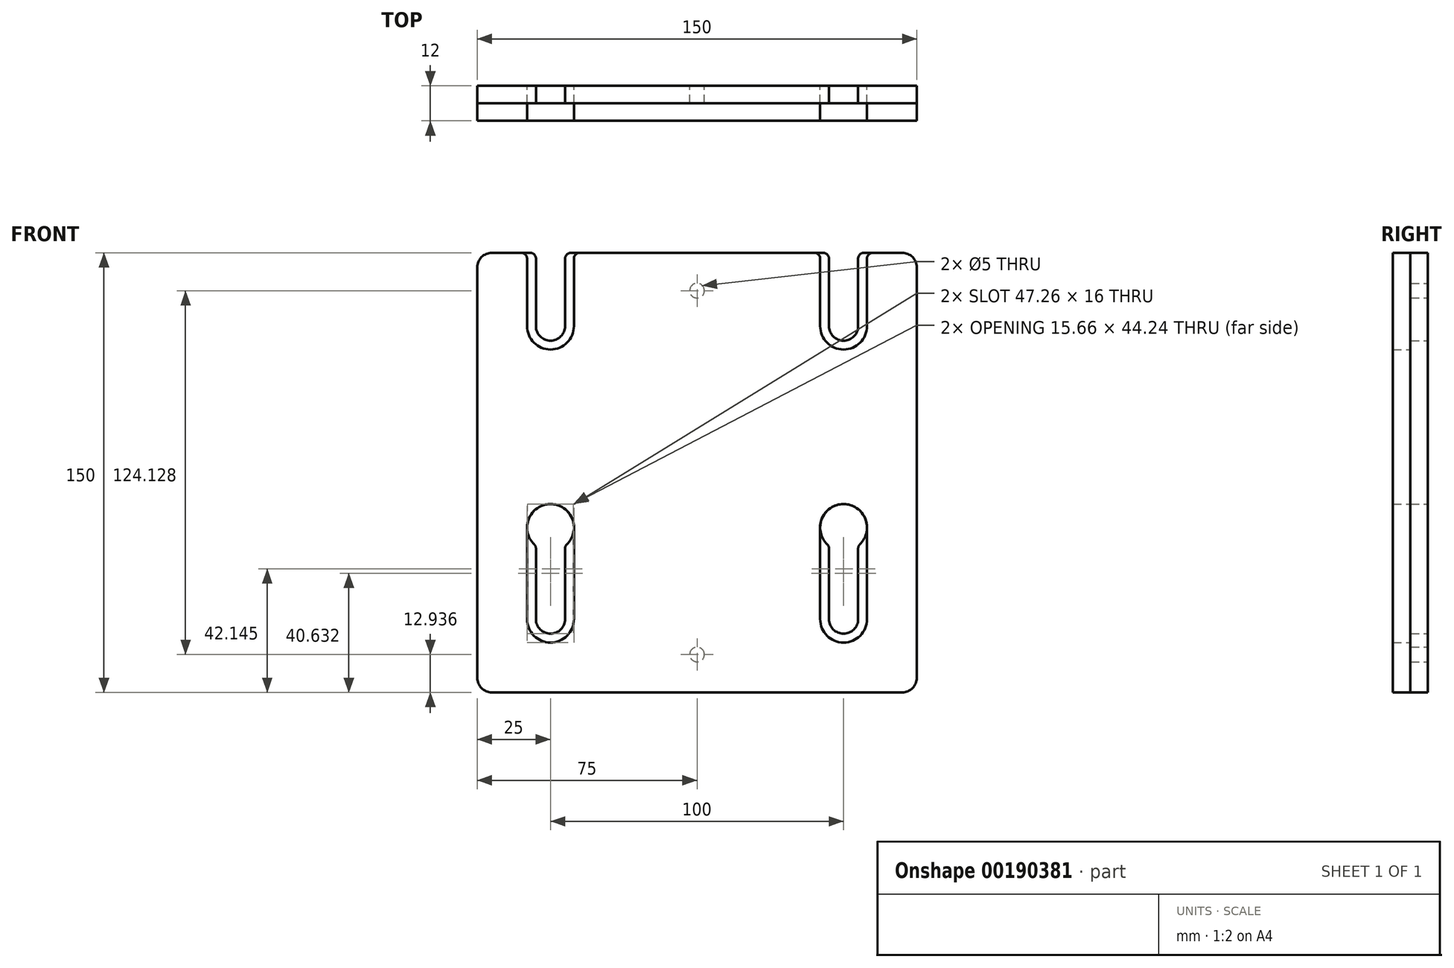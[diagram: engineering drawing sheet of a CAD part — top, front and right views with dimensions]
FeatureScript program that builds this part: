
annotation { "Feature Type Name" : "Feature", "Feature Type Description" : "" }
export const myFeature = defineFeature(function(context is Context, id is Id, definition is map)
    precondition{}
    {
        {
            var Q0;
            Q0=qCreatedBy(makeId("Front.planeOp"),FACE);
            var sketch = newSketch(context, id + "F0", { "sketchPlane" : qUnion([Q0])});
            skLineSegment(sketch, "E0.bottom", {"start": v(70, -75) * mm, "end": v(-70, -75) * mm});
            skLineSegment(sketch, "E0.top", {"start": v(70, 75) * mm, "end": v(56.98, 75) * mm});
            skLineSegment(sketch, "E0.left", {"start": v(75, -70) * mm, "end": v(75, 70) * mm});
            skLineSegment(sketch, "E0.right", {"start": v(-75, -70) * mm, "end": v(-75, 70) * mm});
            skPoint(sketch, "E0.middle", {"position": v(0, 0) * mm});
            skArc(sketch, "E1", {"start": v(-54.98, 50) * mm, "mid": v(-50, 45.03) * mm, "end": v(-45.03, 50) * mm});
            skArc(sketch, "E2.MirrorC", {"start": v(54.98, 50) * mm, "mid": v(50, 45.03) * mm, "end": v(45.03, 50) * mm});
            skArc(sketch, "E3.MirrorC", {"start": v(-45.03, -50) * mm, "mid": v(-50, -54.98) * mm, "end": v(-54.98, -50) * mm});
            skArc(sketch, "E4.MirrorC", {"start": v(45.03, -50) * mm, "mid": v(50, -54.98) * mm, "end": v(54.98, -50) * mm});
            skPoint(sketch, "E5.visualSharp", {"position": v(-75, 75) * mm});
            skArc(sketch, "E5.filletArc", {"start": v(-70, 75) * mm, "mid": v(-73.54, 73.54) * mm, "end": v(-75, 70) * mm});
            skPoint(sketch, "E6.visualSharp", {"position": v(-75, -75) * mm});
            skArc(sketch, "E6.filletArc", {"start": v(-75, -70) * mm, "mid": v(-73.54, -73.54) * mm, "end": v(-70, -75) * mm});
            skPoint(sketch, "E7.visualSharp", {"position": v(75, -75) * mm});
            skArc(sketch, "E7.filletArc", {"start": v(70, -75) * mm, "mid": v(73.54, -73.54) * mm, "end": v(75, -70) * mm});
            skLineSegment(sketch, "E8", {"start": v(-45.03, 50) * mm, "end": v(-45.03, 73) * mm});
            skLineSegment(sketch, "E9", {"start": v(-54.98, 50) * mm, "end": v(-54.98, 73) * mm});
            skArc(sketch, "E10", {"start": v(-44.42, -24.47) * mm, "mid": v(-50, -10.74) * mm, "end": v(-55.58, -24.47) * mm});
            skLineSegment(sketch, "E11", {"start": v(-45.03, -50) * mm, "end": v(-45.03, -25.9) * mm});
            skLineSegment(sketch, "E12", {"start": v(-54.98, -50) * mm, "end": v(-54.98, -25.9) * mm});
            skLineSegment(sketch, "E13.MirrorCS", {"start": v(45.03, 50) * mm, "end": v(45.03, 73) * mm});
            skLineSegment(sketch, "E14.MirrorCS", {"start": v(54.98, 50) * mm, "end": v(54.98, 73) * mm});
            skArc(sketch, "E15.MirrorCS", {"start": v(44.42, -24.47) * mm, "mid": v(50, -10.74) * mm, "end": v(55.58, -24.47) * mm});
            skLineSegment(sketch, "E16.MirrorCS", {"start": v(45.03, -50) * mm, "end": v(45.03, -25.9) * mm});
            skLineSegment(sketch, "E17.MirrorCS", {"start": v(54.98, -50) * mm, "end": v(54.98, -25.9) * mm});
            skLineSegment(sketch, "E18.trimOffspring", {"start": v(-56.98, 75) * mm, "end": v(-70, 75) * mm});
            skLineSegment(sketch, "E19.trimOffspring", {"start": v(43.03, 75) * mm, "end": v(-43.03, 75) * mm});
            skPoint(sketch, "E20.visualSharp", {"position": v(-54.98, 75) * mm});
            skArc(sketch, "E20.filletArc", {"start": v(-54.98, 73) * mm, "mid": v(-55.56, 74.41) * mm, "end": v(-56.98, 75) * mm});
            skPoint(sketch, "E21.visualSharp", {"position": v(-45.03, 75) * mm});
            skArc(sketch, "E21.filletArc", {"start": v(-43.03, 75) * mm, "mid": v(-44.44, 74.41) * mm, "end": v(-45.03, 73) * mm});
            skPoint(sketch, "E22.visualSharp", {"position": v(45.03, 75) * mm});
            skArc(sketch, "E22.filletArc", {"start": v(45.03, 73) * mm, "mid": v(44.44, 74.41) * mm, "end": v(43.03, 75) * mm});
            skPoint(sketch, "E23.visualSharp", {"position": v(54.98, 75) * mm});
            skArc(sketch, "E23.filletArc", {"start": v(56.98, 75) * mm, "mid": v(55.56, 74.41) * mm, "end": v(54.98, 73) * mm});
            skPoint(sketch, "E24.visualSharp", {"position": v(75, 75) * mm});
            skArc(sketch, "E24.filletArc", {"start": v(75, 70) * mm, "mid": v(73.54, 73.54) * mm, "end": v(70, 75) * mm});
            skPoint(sketch, "E25.visualSharp", {"position": v(-54.98, -25) * mm});
            skArc(sketch, "E25.filletArc", {"start": v(-54.98, -25.9) * mm, "mid": v(-55.13, -25.12) * mm, "end": v(-55.58, -24.47) * mm});
            skPoint(sketch, "E26.visualSharp", {"position": v(-45.03, -25) * mm});
            skArc(sketch, "E26.filletArc", {"start": v(-44.42, -24.47) * mm, "mid": v(-44.87, -25.12) * mm, "end": v(-45.03, -25.9) * mm});
            skPoint(sketch, "E27.visualSharp", {"position": v(45.03, -25) * mm});
            skArc(sketch, "E27.filletArc", {"start": v(45.03, -25.9) * mm, "mid": v(44.87, -25.12) * mm, "end": v(44.42, -24.47) * mm});
            skPoint(sketch, "E28.visualSharp", {"position": v(54.98, -25) * mm});
            skArc(sketch, "E28.filletArc", {"start": v(55.58, -24.47) * mm, "mid": v(55.13, -25.12) * mm, "end": v(54.98, -25.9) * mm});
            skCircle(sketch, "E29", {"center": v(0, 62.06) * mm, "radius": 2.5 * mm});
            skCircle(sketch, "E30.MirrorC", {"center": v(0, -62.06) * mm, "radius": 2.5 * mm});
            skSolve(sketch);
        }
        {
            var Q0;
            Q0 = qSketchRegion(id + "F0", true);
            extrude(context, id + "F1", {"entities" : qUnion([Q0]), "depth" : 6 * mm});
        }
        {
            var Q0;
            Q0=makeQuery(id+"F1.opExtrude","CAP_FACE",FACE,{"disambiguationData":[OSD([sQuery(id+"F0.wireOp",EDGE,"E0.bottom"),sQuery(id+"F0.wireOp",EDGE,"E0.top"),sQuery(id+"F0.wireOp",EDGE,"E0.left"),sQuery(id+"F0.wireOp",EDGE,"E0.right"),sQuery(id+"F0.wireOp",EDGE,"E1"),sQuery(id+"F0.wireOp",EDGE,"E2.MirrorC"),sQuery(id+"F0.wireOp",EDGE,"E3.MirrorC"),sQuery(id+"F0.wireOp",EDGE,"E4.MirrorC"),sQuery(id+"F0.wireOp",EDGE,"E5.filletArc"),sQuery(id+"F0.wireOp",EDGE,"E6.filletArc"),sQuery(id+"F0.wireOp",EDGE,"E7.filletArc"),sQuery(id+"F0.wireOp",EDGE,"E8"),sQuery(id+"F0.wireOp",EDGE,"E9"),sQuery(id+"F0.wireOp",EDGE,"E10"),sQuery(id+"F0.wireOp",EDGE,"E11"),sQuery(id+"F0.wireOp",EDGE,"E12"),sQuery(id+"F0.wireOp",EDGE,"E13.MirrorCS"),sQuery(id+"F0.wireOp",EDGE,"E14.MirrorCS"),sQuery(id+"F0.wireOp",EDGE,"E15.MirrorCS"),sQuery(id+"F0.wireOp",EDGE,"E16.MirrorCS"),sQuery(id+"F0.wireOp",EDGE,"E17.MirrorCS"),sQuery(id+"F0.wireOp",EDGE,"E18.trimOffspring"),sQuery(id+"F0.wireOp",EDGE,"E19.trimOffspring"),sQuery(id+"F0.wireOp",EDGE,"E20.filletArc"),sQuery(id+"F0.wireOp",EDGE,"E21.filletArc"),sQuery(id+"F0.wireOp",EDGE,"E22.filletArc"),sQuery(id+"F0.wireOp",EDGE,"E23.filletArc"),sQuery(id+"F0.wireOp",EDGE,"E24.filletArc"),sQuery(id+"F0.wireOp",EDGE,"E25.filletArc"),sQuery(id+"F0.wireOp",EDGE,"E26.filletArc"),sQuery(id+"F0.wireOp",EDGE,"E27.filletArc"),sQuery(id+"F0.wireOp",EDGE,"E28.filletArc")])],"isStart":false});
            var sketch = newSketch(context, id + "F2", { "sketchPlane" : qUnion([Q0])});
            skPoint(sketch, "E31.0", {"position": v(-50, -10.74) * mm});
            skArc(sketch, "E32.0", {"start": v(-42, -18.74) * mm, "mid": v(-50, -10.74) * mm, "end": v(-58, -18.74) * mm});
            skArc(sketch, "E33.0", {"start": v(-45.03, -50) * mm, "mid": v(-50, -54.98) * mm, "end": v(-54.98, -50) * mm, "construction": true});
            skArc(sketch, "E34.0", {"start": v(-54.98, 50) * mm, "mid": v(-50, 45.03) * mm, "end": v(-45.03, 50) * mm, "construction": true});
            skArc(sketch, "E35", {"start": v(-58, -50) * mm, "mid": v(-50, -58) * mm, "end": v(-42, -50) * mm});
            skLineSegment(sketch, "E36", {"start": v(-58, -18.74) * mm, "end": v(-58, -50) * mm});
            skLineSegment(sketch, "E37", {"start": v(-42, -18.74) * mm, "end": v(-42, -50) * mm});
            skPoint(sketch, "E38.orphan", {"position": v(-55.58, -24.47) * mm});
            skPoint(sketch, "E39.orphan", {"position": v(-44.42, -24.47) * mm});
            skArc(sketch, "E40.MirrorCS", {"start": v(45.03, -50) * mm, "mid": v(50, -54.98) * mm, "end": v(54.98, -50) * mm, "construction": true});
            skPoint(sketch, "E41.MirrorP", {"position": v(44.42, -24.47) * mm});
            skPoint(sketch, "E42.MirrorP", {"position": v(50, -10.74) * mm});
            skArc(sketch, "E43.MirrorCS", {"start": v(42, -18.74) * mm, "mid": v(50, -10.74) * mm, "end": v(58, -18.74) * mm});
            skLineSegment(sketch, "E44.MirrorCS", {"start": v(58, -18.74) * mm, "end": v(58, -50) * mm});
            skPoint(sketch, "E45.MirrorP", {"position": v(55.58, -24.47) * mm});
            skLineSegment(sketch, "E46.MirrorCS", {"start": v(42, -18.74) * mm, "end": v(42, -50) * mm});
            skArc(sketch, "E47.MirrorCS", {"start": v(58, -50) * mm, "mid": v(50, -58) * mm, "end": v(42, -50) * mm});
            skArc(sketch, "E48", {"start": v(-58, 50) * mm, "mid": v(-50, 42) * mm, "end": v(-42, 50) * mm});
            skLineSegment(sketch, "E49", {"start": v(-58, 50) * mm, "end": v(-58, 73) * mm});
            skLineSegment(sketch, "E50", {"start": v(-42, 50) * mm, "end": v(-42, 73) * mm});
            skLineSegment(sketch, "E51.0", {"start": v(-75, -70) * mm, "end": v(-75, 70) * mm});
            skArc(sketch, "E52.0", {"start": v(-70, 75) * mm, "mid": v(-73.54, 73.54) * mm, "end": v(-75, 70) * mm});
            skLineSegment(sketch, "E53.MirrorCS", {"start": v(42, 50) * mm, "end": v(42, 73) * mm});
            skArc(sketch, "E54.MirrorCS", {"start": v(58, 50) * mm, "mid": v(50, 42) * mm, "end": v(42, 50) * mm});
            skLineSegment(sketch, "E55.MirrorCS", {"start": v(58, 50) * mm, "end": v(58, 73) * mm});
            skPoint(sketch, "E56.0", {"position": v(73.54, 73.54) * mm});
            skLineSegment(sketch, "E57.0", {"start": v(75, -70) * mm, "end": v(75, 70) * mm});
            skLineSegment(sketch, "E58.0", {"start": v(70, -75) * mm, "end": v(-70, -75) * mm});
            skArc(sketch, "E59.0", {"start": v(70, -75) * mm, "mid": v(73.54, -73.54) * mm, "end": v(75, -70) * mm});
            skArc(sketch, "E60.0", {"start": v(-75, -70) * mm, "mid": v(-73.54, -73.54) * mm, "end": v(-70, -75) * mm});
            skArc(sketch, "E61.0", {"start": v(75, 70) * mm, "mid": v(73.54, 73.54) * mm, "end": v(70, 75) * mm});
            skLineSegment(sketch, "E62", {"start": v(70, 75) * mm, "end": v(60, 75) * mm});
            skLineSegment(sketch, "E63", {"start": v(40, 75) * mm, "end": v(-40, 75) * mm});
            skLineSegment(sketch, "E64", {"start": v(-60, 75) * mm, "end": v(-70, 75) * mm});
            skPoint(sketch, "E65.visualSharp", {"position": v(-58, 75) * mm});
            skArc(sketch, "E65.filletArc", {"start": v(-58, 73) * mm, "mid": v(-58.59, 74.41) * mm, "end": v(-60, 75) * mm});
            skPoint(sketch, "E66.visualSharp", {"position": v(-42, 75) * mm});
            skArc(sketch, "E66.filletArc", {"start": v(-40, 75) * mm, "mid": v(-41.41, 74.41) * mm, "end": v(-42, 73) * mm});
            skPoint(sketch, "E67.visualSharp", {"position": v(42, 75) * mm});
            skArc(sketch, "E67.filletArc", {"start": v(42, 73) * mm, "mid": v(41.41, 74.41) * mm, "end": v(40, 75) * mm});
            skPoint(sketch, "E68.visualSharp", {"position": v(58, 75) * mm});
            skArc(sketch, "E68.filletArc", {"start": v(60, 75) * mm, "mid": v(58.59, 74.41) * mm, "end": v(58, 73) * mm});
            skSolve(sketch);
        }
        {
            var Q0;
            Q0 = qSketchRegion(id + "F2", true);
            extrude(context, id + "F3", {"entities" : qUnion([Q0]), "depth" : 6 * mm});
        }
    });
